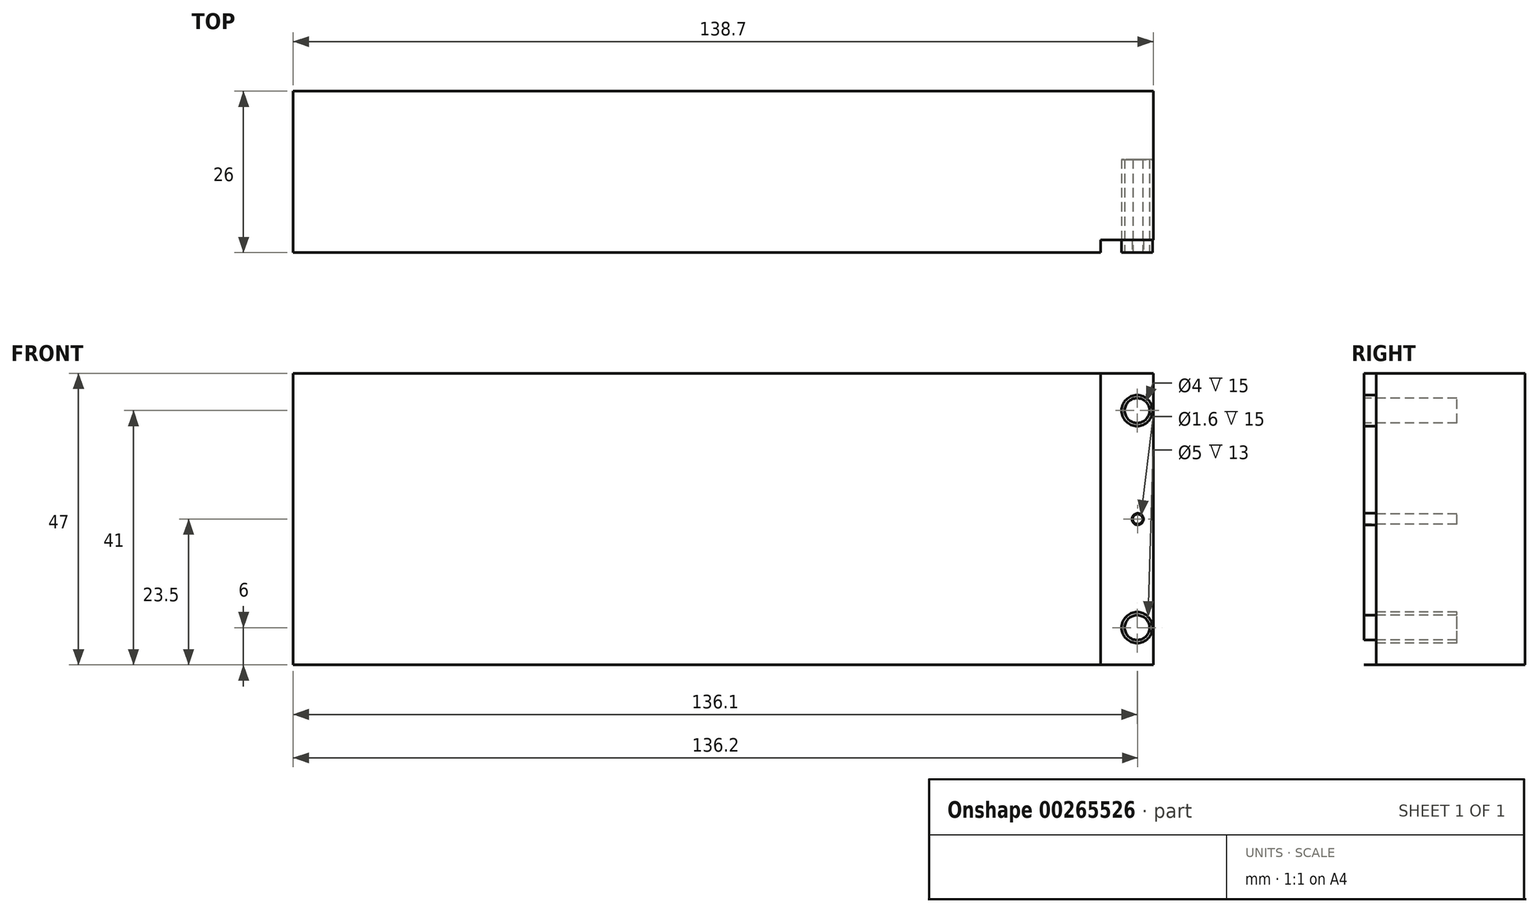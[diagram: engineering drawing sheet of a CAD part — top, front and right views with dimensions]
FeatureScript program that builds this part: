
annotation { "Feature Type Name" : "Feature", "Feature Type Description" : "" }
export const myFeature = defineFeature(function(context is Context, id is Id, definition is map)
    precondition{}
    {
        {
            var Q0;
            Q0=qCreatedBy(makeId("Front.planeOp"),FACE);
            var sketch = newSketch(context, id + "F0", { "sketchPlane" : qUnion([Q0])});
            skLineSegment(sketch, "E0.bottom", {"start": v(69.35, -23.5) * mm, "end": v(-69.35, -23.5) * mm});
            skLineSegment(sketch, "E0.top", {"start": v(69.35, 23.5) * mm, "end": v(-69.35, 23.5) * mm});
            skLineSegment(sketch, "E0.left", {"start": v(69.35, -23.5) * mm, "end": v(69.35, 23.5) * mm});
            skLineSegment(sketch, "E0.right", {"start": v(-69.35, -23.5) * mm, "end": v(-69.35, 23.5) * mm});
            skPoint(sketch, "E0.middle", {"position": v(0, 0) * mm});
            skSolve(sketch);
        }
        {
            var Q0;
            Q0=makeQuery(id+"F0.imprint","IMPRINT",FACE,{"disambiguationData":[TD([[makeQuery(id+"F0.imprint","IMPRINT",EDGE,{"derivedFrom":sQuery(id+"F0.wireOp",EDGE,"E0.bottom")}),-1.0]])]});
            extrude(context, id + "F1", {"entities" : qUnion([Q0]), "depth" : 26 * mm});
        }
        {
            var Q0;
            Q0=makeQuery(id+"F1.opExtrude","CAP_FACE",FACE,{"disambiguationData":[OSD([sQuery(id+"F0.wireOp",EDGE,"E0.bottom"),sQuery(id+"F0.wireOp",EDGE,"E0.top"),sQuery(id+"F0.wireOp",EDGE,"E0.left"),sQuery(id+"F0.wireOp",EDGE,"E0.right")])],"isStart":false});
            var sketch = newSketch(context, id + "F2", { "sketchPlane" : qUnion([Q0])});
            skLineSegment(sketch, "E1.bottom", {"start": v(69.35, 23.5) * mm, "end": v(60.85, 23.5) * mm});
            skLineSegment(sketch, "E1.top", {"start": v(69.35, -23.5) * mm, "end": v(60.85, -23.5) * mm});
            skLineSegment(sketch, "E1.left", {"start": v(69.35, 23.5) * mm, "end": v(69.35, -23.5) * mm});
            skLineSegment(sketch, "E1.right", {"start": v(60.85, 23.5) * mm, "end": v(60.85, -23.5) * mm});
            skLineSegment(sketch, "E2", {"start": v(62.9, 23.5) * mm, "end": v(62.9, 17.5) * mm, "construction": true});
            skLineSegment(sketch, "E3", {"start": v(69.35, 0) * mm, "end": v(7.57, 0) * mm, "construction": true});
            skPoint(sketch, "E3.endSnap0", {"position": v(69.35, 0) * mm});
            skLineSegment(sketch, "E4.MirrorCS", {"start": v(62.9, -23.5) * mm, "end": v(62.9, -17.5) * mm, "construction": true});
            skCircle(sketch, "E5", {"center": v(66.75, 17.5) * mm, "radius": 2.5 * mm});
            skCircle(sketch, "E6", {"center": v(66.75, 17.5) * mm, "radius": 2 * mm});
            skCircle(sketch, "E7.MirrorC", {"center": v(66.75, -17.5) * mm, "radius": 2.5 * mm});
            skCircle(sketch, "E8.MirrorC", {"center": v(66.75, -17.5) * mm, "radius": 2 * mm});
            skCircle(sketch, "E9", {"center": v(66.85, 0) * mm, "radius": 0.93 * mm});
            skLineSegment(sketch, "E10", {"start": v(66.75, 17.5) * mm, "end": v(69.35, 17.5) * mm, "construction": true});
            skCircle(sketch, "E11", {"center": v(66.85, 0) * mm, "radius": 0.8 * mm});
            skSolve(sketch);
        }
        {
            var Q0;
            Q0=makeQuery(id+"F2.imprint","IMPRINT",FACE,{"disambiguationData":[TD([[makeQuery(id+"F2.imprint","IMPRINT",EDGE,{"derivedFrom":sQuery(id+"F2.wireOp",EDGE,"E1.bottom")}),1.0]])]});
            extrude(context, id + "F3", {"entities" : qUnion([Q0]), "operationType" : NewBodyOperationType.REMOVE, "oppositeDirection" : true, "depth" : 2 * mm});
        }
        {
            var Q0;
            Q0=makeQuery(id+"F2.imprint","IMPRINT",FACE,{"disambiguationData":[TD([[makeQuery(id+"F2.imprint","IMPRINT",EDGE,{"derivedFrom":sQuery(id+"F2.wireOp",EDGE,"E11")}),1.0]])]});
            var Q1;
            Q1=makeQuery(id+"F2.imprint","IMPRINT",FACE,{"disambiguationData":[TD([[makeQuery(id+"F2.imprint","IMPRINT",EDGE,{"derivedFrom":sQuery(id+"F2.wireOp",EDGE,"E6")}),1.0]])]});
            var Q2;
            Q2=makeQuery(id+"F2.imprint","IMPRINT",FACE,{"disambiguationData":[TD([[makeQuery(id+"F2.imprint","IMPRINT",EDGE,{"derivedFrom":sQuery(id+"F2.wireOp",EDGE,"E8.MirrorC")}),-1.0]])]});
            extrude(context, id + "F4", {"entities" : qUnion([Q0, Q1, Q2]), "operationType" : NewBodyOperationType.REMOVE, "oppositeDirection" : true, "depth" : 15 * mm});
        }
    });
